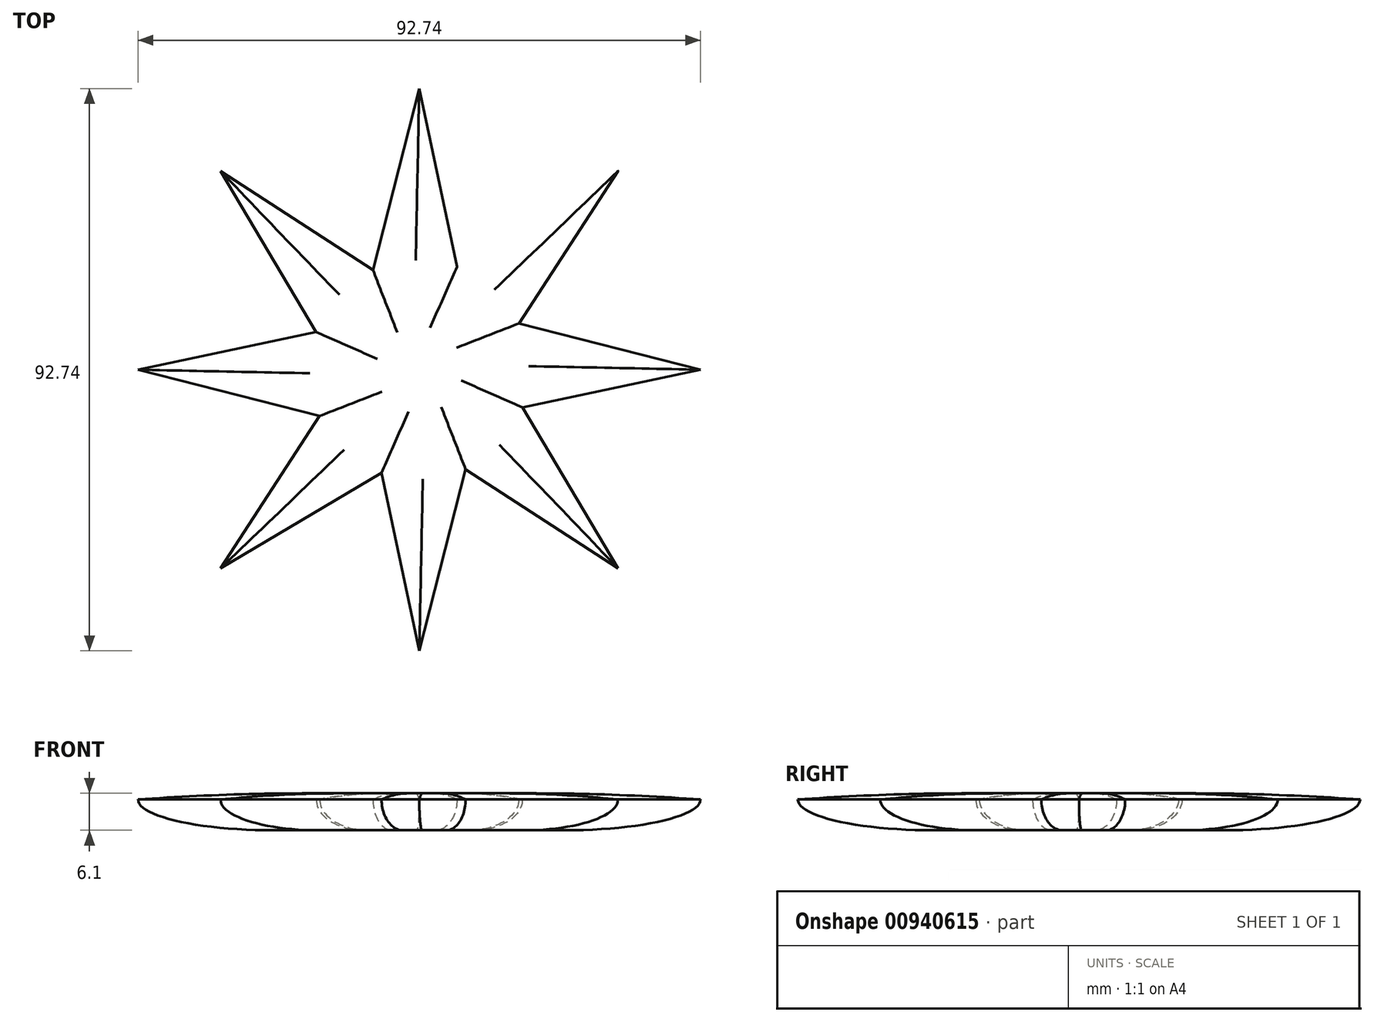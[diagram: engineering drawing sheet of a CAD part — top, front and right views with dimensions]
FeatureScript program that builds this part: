
annotation { "Feature Type Name" : "Feature", "Feature Type Description" : "" }
export const myFeature = defineFeature(function(context is Context, id is Id, definition is map)
    precondition{}
    {
        {
            var Q0;
            Q0=qCreatedBy(makeId("Top.planeOp"),FACE);
            var sketch = newSketch(context, id + "F0", { "sketchPlane" : qUnion([Q0])});
            skLineSegment(sketch, "E0", {"start": v(0, 46.37) * mm, "end": v(6.21, 17) * mm});
            skLineSegment(sketch, "E1.1.1", {"start": v(-32.79, 32.79) * mm, "end": v(-7.63, 16.42) * mm});
            skLineSegment(sketch, "E1.2.1", {"start": v(-46.37, 0) * mm, "end": v(-17, 6.21) * mm});
            skLineSegment(sketch, "E1.3.1", {"start": v(-32.79, -32.79) * mm, "end": v(-16.42, -7.63) * mm});
            skLineSegment(sketch, "E1.4.1", {"start": v(0, -46.37) * mm, "end": v(-6.21, -17) * mm});
            skLineSegment(sketch, "E1.5.1", {"start": v(32.79, -32.79) * mm, "end": v(7.63, -16.42) * mm});
            skLineSegment(sketch, "E1.6.1", {"start": v(46.37, 0) * mm, "end": v(17, -6.21) * mm});
            skLineSegment(sketch, "E1.7.1", {"start": v(32.79, 32.79) * mm, "end": v(16.42, 7.63) * mm});
            skPoint(sketch, "E1.center", {"position": v(0, 0) * mm});
            skLineSegment(sketch, "E2.trimOffspring", {"start": v(-16.42, -7.63) * mm, "end": v(-46.37, 0) * mm});
            skLineSegment(sketch, "E3.trimOffspring", {"start": v(-6.21, -17) * mm, "end": v(-32.79, -32.79) * mm});
            skLineSegment(sketch, "E4.trimOffspring", {"start": v(7.63, -16.42) * mm, "end": v(0, -46.37) * mm});
            skLineSegment(sketch, "E5.trimOffspring", {"start": v(17, -6.21) * mm, "end": v(32.79, -32.79) * mm});
            skLineSegment(sketch, "E6.trimOffspring", {"start": v(16.42, 7.63) * mm, "end": v(46.37, 0) * mm});
            skLineSegment(sketch, "E7.trimOffspring", {"start": v(6.21, 17) * mm, "end": v(32.79, 32.79) * mm});
            skLineSegment(sketch, "E8.trimOffspring", {"start": v(-7.63, 16.42) * mm, "end": v(0, 46.37) * mm});
            skLineSegment(sketch, "E9.trimOffspring", {"start": v(-17, 6.21) * mm, "end": v(-32.79, 32.79) * mm});
            skSolve(sketch);
        }
        {
            var Q0;
            Q0 = qSketchRegion(id + "F0", true);
            extrude(context, id + "F1", {"entities" : qUnion([Q0]), "depth" : 6.1 * mm, "offsetDistance" : 25.4 * mm});
        }
        {
            var Q0;
            Q0=makeQuery(id+"F1.opExtrude","CAP_FACE",FACE,{"disambiguationData":[OSD([sQuery(id+"F0.wireOp",EDGE,"E0"),sQuery(id+"F0.wireOp",EDGE,"E1.1.1"),sQuery(id+"F0.wireOp",EDGE,"E1.2.1"),sQuery(id+"F0.wireOp",EDGE,"E1.3.1"),sQuery(id+"F0.wireOp",EDGE,"E1.4.1"),sQuery(id+"F0.wireOp",EDGE,"E1.5.1"),sQuery(id+"F0.wireOp",EDGE,"E1.6.1"),sQuery(id+"F0.wireOp",EDGE,"E1.7.1"),sQuery(id+"F0.wireOp",EDGE,"E2.trimOffspring"),sQuery(id+"F0.wireOp",EDGE,"E3.trimOffspring"),sQuery(id+"F0.wireOp",EDGE,"E4.trimOffspring"),sQuery(id+"F0.wireOp",EDGE,"E5.trimOffspring"),sQuery(id+"F0.wireOp",EDGE,"E6.trimOffspring"),sQuery(id+"F0.wireOp",EDGE,"E7.trimOffspring"),sQuery(id+"F0.wireOp",EDGE,"E8.trimOffspring"),sQuery(id+"F0.wireOp",EDGE,"E9.trimOffspring")])],"isStart":true});
            fillet(context, id + "F2", {"entities" : qUnion([Q0]), "radius" : 5.08 * mm, "tangentPropagation" : true, "allowEdgeOverflow" : false});
        }
        {
            var Q0;
            Q0=makeQuery(id+"F1.opExtrude","CAP_EDGE",EDGE,{"disambiguationData":[OSD([sQuery(id+"F0.wireOp",EDGE,"E1.5.1")])],"isStart":false});
            var Q1;
            Q1=makeQuery(id+"F1.opExtrude","CAP_EDGE",EDGE,{"disambiguationData":[OSD([sQuery(id+"F0.wireOp",EDGE,"E5.trimOffspring")])],"isStart":false});
            var Q2;
            Q2=makeQuery(id+"F1.opExtrude","CAP_EDGE",EDGE,{"disambiguationData":[OSD([sQuery(id+"F0.wireOp",EDGE,"E1.6.1")])],"isStart":false});
            var Q3;
            Q3=makeQuery(id+"F1.opExtrude","CAP_EDGE",EDGE,{"disambiguationData":[OSD([sQuery(id+"F0.wireOp",EDGE,"E6.trimOffspring")])],"isStart":false});
            var Q4;
            Q4=makeQuery(id+"F1.opExtrude","CAP_EDGE",EDGE,{"disambiguationData":[OSD([sQuery(id+"F0.wireOp",EDGE,"E1.7.1")])],"isStart":false});
            var Q5;
            Q5=makeQuery(id+"F1.opExtrude","CAP_EDGE",EDGE,{"disambiguationData":[OSD([sQuery(id+"F0.wireOp",EDGE,"E7.trimOffspring")])],"isStart":false});
            var Q6;
            {var subQ0=sQuery(id+"F0.wireOp",EDGE,"E0");Q6=makeQuery(id+"F2.opFillet","BLEND_EDGE",EDGE,{"blendedFrom":[makeQuery(id+"F1.opExtrude","CAP_EDGE",EDGE,{"disambiguationData":[OSD([subQ0])],"isStart":true}),makeQuery(id+"F1.opExtrude","SWEPT_FACE",FACE,{"disambiguationData":[OSD([subQ0])]})],"blendedInto":[makeQuery(id+"F1.opExtrude","SWEPT_FACE",FACE,{"disambiguationData":[OSD([subQ0])]})]});}
            var Q7;
            Q7=makeQuery(id+"F1.opExtrude","CAP_EDGE",EDGE,{"disambiguationData":[OSD([sQuery(id+"F0.wireOp",EDGE,"E8.trimOffspring")])],"isStart":false});
            var Q8;
            Q8=makeQuery(id+"F1.opExtrude","CAP_EDGE",EDGE,{"disambiguationData":[OSD([sQuery(id+"F0.wireOp",EDGE,"E1.1.1")])],"isStart":false});
            var Q9;
            Q9=makeQuery(id+"F1.opExtrude","CAP_EDGE",EDGE,{"disambiguationData":[OSD([sQuery(id+"F0.wireOp",EDGE,"E9.trimOffspring")])],"isStart":false});
            var Q10;
            Q10=makeQuery(id+"F1.opExtrude","CAP_EDGE",EDGE,{"disambiguationData":[OSD([sQuery(id+"F0.wireOp",EDGE,"E1.2.1")])],"isStart":false});
            var Q11;
            Q11=makeQuery(id+"F1.opExtrude","CAP_EDGE",EDGE,{"disambiguationData":[OSD([sQuery(id+"F0.wireOp",EDGE,"E1.3.1")])],"isStart":false});
            var Q12;
            Q12=makeQuery(id+"F1.opExtrude","CAP_EDGE",EDGE,{"disambiguationData":[OSD([sQuery(id+"F0.wireOp",EDGE,"E3.trimOffspring")])],"isStart":false});
            var Q13;
            Q13=makeQuery(id+"F1.opExtrude","CAP_EDGE",EDGE,{"disambiguationData":[OSD([sQuery(id+"F0.wireOp",EDGE,"E2.trimOffspring")])],"isStart":false});
            var Q14;
            Q14=makeQuery(id+"F1.opExtrude","CAP_EDGE",EDGE,{"disambiguationData":[OSD([sQuery(id+"F0.wireOp",EDGE,"E1.4.1")])],"isStart":false});
            var Q15;
            Q15=makeQuery(id+"F1.opExtrude","CAP_EDGE",EDGE,{"disambiguationData":[OSD([sQuery(id+"F0.wireOp",EDGE,"E4.trimOffspring")])],"isStart":false});
            var Q16;
            Q16=makeQuery(id+"F1.opExtrude","CAP_EDGE",EDGE,{"disambiguationData":[OSD([sQuery(id+"F0.wireOp",EDGE,"E0")])],"isStart":false});
            fillet(context, id + "F3", {"entities" : qUnion([Q0, Q1, Q2, Q3, Q4, Q5, Q6, Q7, Q8, Q9, Q10, Q11, Q12, Q13, Q14, Q15, Q16]), "radius" : 20.85 * mm, "tangentPropagation" : true, "allowEdgeOverflow" : false});
        }
        {
            var Q0;
            {var subQ0=sQuery(id+"F0.wireOp",EDGE,"E7.trimOffspring");Q0=makeQuery(id+"F3.opFillet","BLEND_EDGE",EDGE,{"blendedFrom":[makeQuery(id+"F1.opExtrude","CAP_EDGE",EDGE,{"disambiguationData":[OSD([subQ0])],"isStart":false}),makeQuery(id+"F2.opFillet","BLEND_FACE",FACE,{"disambiguationData":[OSD([subQ0])]})],"blendedInto":[makeQuery(id+"F2.opFillet","BLEND_FACE",FACE,{"disambiguationData":[OSD([subQ0])]})]});}
            fillet(context, id + "F4", {"entities" : qUnion([Q0]), "radius" : 0.04 * mm, "tangentPropagation" : true, "allowEdgeOverflow" : false});
        }
    });
